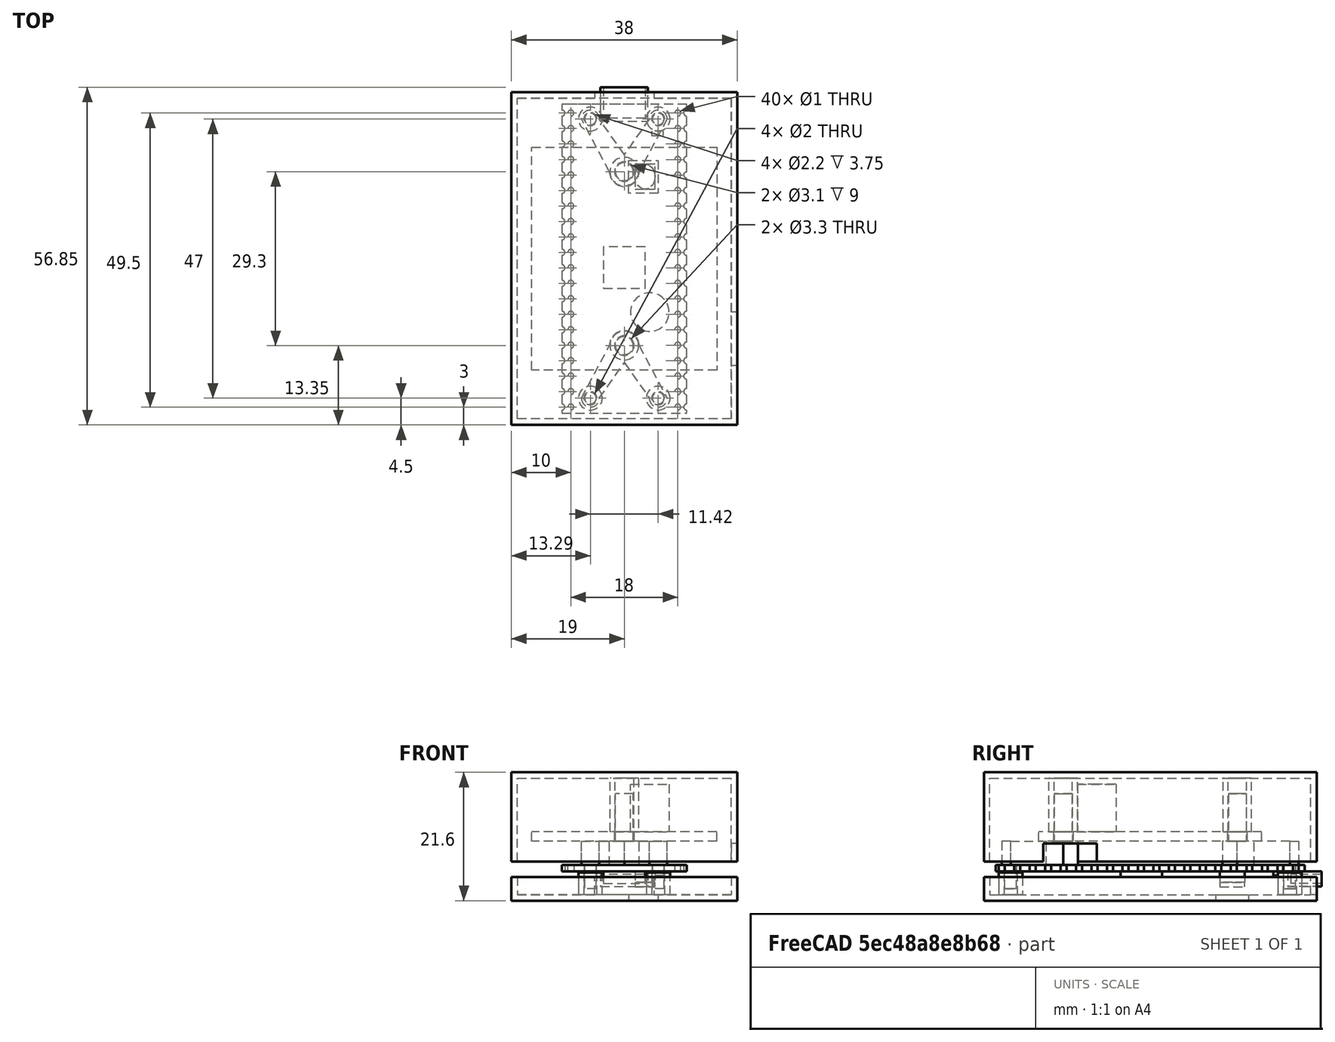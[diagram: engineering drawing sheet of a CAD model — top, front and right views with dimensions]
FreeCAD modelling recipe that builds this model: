
FCSTD DOCUMENT  (FreeCAD 0.19R24366 (Git))
Label: electronics_case
License: All rights reserved
LicenseURL: http://en.wikipedia.org/wiki/All_rights_reserved
objects: Sketcher::SketchObject×29, PartDesign::Pad×18, PartDesign::Pocket×11, PartDesign::Mirrored×7, PartDesign::Body×6, PartDesign::MultiTransform×3, Mesh::Feature×3, PartDesign::LinearPattern×2
note: 105 computed .brp shape members not serialized (recipe doc carries the construction recipe); baked Part::Feature solids carry a one-line shape summary decoded from their .brp

FEATURE [Sketcher::SketchObject] Sketch
  FullyConstrained = true
  MapMode = 5
  Support = -> [XY_Plane]
  sketch-geometry (4):
    g0: LineSegment StartX=-10.5 StartY=26 StartZ=0 EndX=10.5 EndY=26 EndZ=0
    g1: LineSegment StartX=10.5 StartY=26 StartZ=0 EndX=10.5 EndY=-26 EndZ=0
    g2: LineSegment StartX=10.5 StartY=-26 StartZ=0 EndX=-10.5 EndY=-26 EndZ=0
    g3: LineSegment StartX=-10.5 StartY=-26 StartZ=0 EndX=-10.5 EndY=26 EndZ=0
  constraints (11):
    c: Coincident(g0,g1)
    c: Coincident(g1,g2)
    c: Coincident(g2,g3)
    c: Coincident(g3,g0)
    c: Horizontal(g0)
    c: Horizontal(g2)
    c: Vertical(g1)
    c: Vertical(g3)
    c: Symmetric(g1,g0,g-1)
    c: DistanceY(g1,g1) = 52
    c: DistanceX(g0,g0) = 21
FEATURE [PartDesign::Pad] Pad
  Direction = (1,1,1)
  Length = 1.1
  Length2 = 100
  Profile = -> Sketch
  Refine = true
  Type = 0
FEATURE [Sketcher::SketchObject] Sketch001
  FullyConstrained = true
  MapMode = 5
  Placement = pos=(0,0,1.1) rot=(0,0,1;0rad)
  Support = -> [Pad]
  expr: Constraints[2] = 11.42 / 2
  sketch-geometry (1):
    g0: Circle CenterX=-5.71 CenterY=23.5 CenterZ=0 NormalX=0 NormalY=0 NormalZ=1 AngleXU=0 Radius=1
  constraints (3):
    c: Diameter(g0) = 2
    c: DistanceY(g-1,g0) = 23.5
    c: DistanceX(g0,g-1) = 5.71
FEATURE [PartDesign::Pocket] Pocket
  BaseFeature = -> Pad
  Length = 5
  Length2 = 100
  Profile = -> Sketch001
  Refine = true
  Type = 1
FEATURE [PartDesign::Mirrored] Mirrored
  MirrorPlane = -> Sketch001 [V_Axis]
  Refine = true
FEATURE [PartDesign::Mirrored] Mirrored001
  MirrorPlane = -> Sketch001 [H_Axis]
  Refine = true
FEATURE [PartDesign::MultiTransform] MultiTransform
  BaseFeature = -> Pocket
  Originals = -> [Pocket]
  Refine = true
  Transformations = -> [Mirrored,Mirrored001]
FEATURE [Sketcher::SketchObject] Sketch002
  ExternalGeometry = -> [MultiTransform]
  FullyConstrained = true
  MapMode = 5
  Support = -> [XY_Plane]
  sketch-geometry (5):
    g0: LineSegment StartX=-4 StartY=28.85 StartZ=0 EndX=4 EndY=28.85 EndZ=0
    g1: LineSegment StartX=4 StartY=28.85 StartZ=0 EndX=4 EndY=23.15 EndZ=0
    g2: LineSegment StartX=4 StartY=23.15 StartZ=0 EndX=-4 EndY=23.15 EndZ=0
    g3: LineSegment StartX=-4 StartY=23.15 StartZ=0 EndX=-4 EndY=28.85 EndZ=0
    g4: GeomPoint X=-2e-16 Y=26 Z=0
  constraints (12):
    c: Coincident(g0,g1)
    c: Coincident(g1,g2)
    c: Coincident(g2,g3)
    c: Coincident(g3,g0)
    c: Horizontal(g0)
    c: Horizontal(g2)
    c: Vertical(g1)
    c: Vertical(g3)
    c: Symmetric(g-3,g-3,g4)
    c: Symmetric(g1,g0,g4)
    c: DistanceX(g0,g0) = 8
    c: DistanceY(g3,g3) = 5.7
FEATURE [PartDesign::Pad] Pad001
  BaseFeature = -> MultiTransform
  Direction = (1,1,1)
  Length = 3.6
  Length2 = 100
  Profile = -> Sketch002
  Refine = true
  Type = 0
FEATURE [Sketcher::SketchObject] Sketch004
  ExternalGeometry = -> [Pad001]
  FullyConstrained = true
  MapMode = 5
  Placement = pos=(0,0,1.1) rot=(0,0,1;0rad)
  Support = -> [Pad001]
  sketch-geometry (4):
    g0: LineSegment StartX=-5.15 StartY=15.9 StartZ=0 EndX=-1.8 EndY=15.9 EndZ=0
    g1: LineSegment StartX=-1.8 StartY=15.9 StartZ=0 EndX=-1.8 EndY=11.7 EndZ=0
    g2: LineSegment StartX=-1.8 StartY=11.7 StartZ=0 EndX=-5.15 EndY=11.7 EndZ=0
    g3: LineSegment StartX=-5.15 StartY=11.7 StartZ=0 EndX=-5.15 EndY=15.9 EndZ=0
  constraints (12):
    c: Coincident(g0,g1)
    c: Coincident(g1,g2)
    c: Coincident(g2,g3)
    c: Coincident(g3,g0)
    c: Horizontal(g0)
    c: Horizontal(g2)
    c: Vertical(g1)
    c: Vertical(g3)
    c: DistanceY(g1,g1) = 4.2
    c: DistanceX(g0,g0) = 3.35
    c: DistanceX(g-3,g2) = 5.35
    c: DistanceY(g0,g-3) = 10.1
FEATURE [PartDesign::Pad] Pad002
  BaseFeature = -> Pad001
  Direction = (1,1,1)
  Length = 1.8
  Length2 = 100
  Profile = -> Sketch004
  Refine = true
  Type = 0
FEATURE [Sketcher::SketchObject] Sketch005
  ExternalGeometry = -> [Pad002]
  FullyConstrained = true
  MapMode = 5
  Placement = pos=(0,0,2.9) rot=(0,0,1;0rad)
  Support = -> [Pad002]
  sketch-geometry (5):
    g0: Ellipse CenterX=-3.475 CenterY=13.8 CenterZ=0 NormalX=0 NormalY=0 NormalZ=1 MajorRadius=2.1 MinorRadius=1.675 AngleXU=-1.5708
    g1: LineSegment StartX=-3.475 StartY=11.7 StartZ=0 EndX=-3.475 EndY=15.9 EndZ=0
    g2: LineSegment StartX=-1.8 StartY=13.8 StartZ=0 EndX=-5.15 EndY=13.8 EndZ=0
    g3: GeomPoint X=-3.475 Y=12.5334 Z=0
    g4: GeomPoint X=-3.475 Y=15.0666 Z=0
  constraints (4):
    c: InternalAlignment(g1-g4 -> g0) x4
    c: Symmetric(g-5,g-6,g0)
    c: Symmetric(g-6,g-5,g1)
    c: Symmetric(g-6,g-6,g2)
FEATURE [PartDesign::Pad] Pad003
  BaseFeature = -> Pad002
  Direction = (1,1,1)
  Length = 0.8
  Length2 = 100
  Profile = -> Sketch005
  Refine = true
  Type = 0
FEATURE [Sketcher::SketchObject] Sketch006
  ExternalGeometry = -> [Pad003]
  FullyConstrained = true
  MapMode = 5
  Placement = pos=(0,0,1.1) rot=(0,0,1;0rad)
  Support = -> [Pad003]
  sketch-geometry (4):
    g0: LineSegment StartX=-6.6 StartY=21.5 StartZ=0 EndX=-4.6 EndY=21.5 EndZ=0
    g1: LineSegment StartX=-4.6 StartY=21.5 StartZ=0 EndX=-4.6 EndY=20.7 EndZ=0
    g2: LineSegment StartX=-4.6 StartY=20.7 StartZ=0 EndX=-6.6 EndY=20.7 EndZ=0
    g3: LineSegment StartX=-6.6 StartY=20.7 StartZ=0 EndX=-6.6 EndY=21.5 EndZ=0
  constraints (12):
    c: Coincident(g0,g1)
    c: Coincident(g1,g2)
    c: Coincident(g2,g3)
    c: Coincident(g3,g0)
    c: Horizontal(g0)
    c: Horizontal(g2)
    c: Vertical(g1)
    c: Vertical(g3)
    c: DistanceX(g0,g0) = 2
    c: DistanceY(g3,g3) = 0.8
    c: DistanceX(g-3,g0) = 3.9
    c: DistanceY(g0,g-3) = 4.5
FEATURE [PartDesign::Pad] Pad004
  BaseFeature = -> Pad003
  Direction = (1,1,1)
  Length = 0.7
  Length2 = 100
  Profile = -> Sketch006
  Refine = true
  Type = 0
FEATURE [Sketcher::SketchObject] Sketch007
  ExternalGeometry = -> [Pad004]
  FullyConstrained = true
  MapMode = 5
  Placement = pos=(0,0,1.1) rot=(0,0,1;0rad)
  Support = -> [Pad004]
  sketch-geometry (4):
    g0: LineSegment StartX=-3.5 StartY=2 StartZ=0 EndX=3.5 EndY=2 EndZ=0
    g1: LineSegment StartX=3.5 StartY=2 StartZ=0 EndX=3.5 EndY=-5 EndZ=0
    g2: LineSegment StartX=3.5 StartY=-5 StartZ=0 EndX=-3.5 EndY=-5 EndZ=0
    g3: LineSegment StartX=-3.5 StartY=-5 StartZ=0 EndX=-3.5 EndY=2 EndZ=0
  constraints (12):
    c: Coincident(g0,g1)
    c: Coincident(g1,g2)
    c: Coincident(g2,g3)
    c: Coincident(g3,g0)
    c: Horizontal(g0)
    c: Horizontal(g2)
    c: Vertical(g1)
    c: Vertical(g3)
    c: DistanceY(g1,g1) = 7
    c: DistanceX(g0,g0) = 7
    c: DistanceX(g-3,g2) = 7
    c: DistanceY(g-3,g2) = 21
FEATURE [PartDesign::Pad] Pad005
  BaseFeature = -> Pad004
  Direction = (1,1,1)
  Length = 0.9
  Length2 = 100
  Profile = -> Sketch007
  Refine = true
  Type = 0
FEATURE [Sketcher::SketchObject] Sketch009
  ExternalGeometry = -> [Pad005]
  FullyConstrained = true
  MapMode = 5
  Support = -> [XY_Plane]
  sketch-geometry (1):
    g0: Circle CenterX=-9 CenterY=24.5 CenterZ=0 NormalX=0 NormalY=0 NormalZ=1 AngleXU=0 Radius=0.5
  constraints (3):
    c: Diameter(g0) = 1
    c: DistanceY(g0,g-3) = 1.5
    c: DistanceX(g-3,g0) = 1.5
FEATURE [PartDesign::Pocket] Pocket001
  BaseFeature = -> Pad005
  Length = 5
  Length2 = 100
  Profile = -> Sketch009
  Refine = true
  Reversed = true
  Type = 1
FEATURE [PartDesign::LinearPattern] LinearPattern
  Direction = -> Y_Axis
  Length = 49.5
  Occurrences = 20
  Refine = true
  Reversed = true
  expr: Length = 52 - 2.5
FEATURE [PartDesign::Mirrored] Mirrored002
  MirrorPlane = -> Sketch009 [V_Axis]
  Refine = true
FEATURE [PartDesign::MultiTransform] MultiTransform001
  BaseFeature = -> Pocket001
  Originals = -> [Pocket001]
  Refine = true
  Transformations = -> [LinearPattern,Mirrored002]
FEATURE [Sketcher::SketchObject] Sketch010
  ExternalGeometry = -> [MultiTransform001]
  FullyConstrained = true
  MapMode = 5
  Placement = pos=(0,0,1.1) rot=(0,0,1;0rad)
  Support = -> [MultiTransform001]
  sketch-geometry (1):
    g0: Circle CenterX=-10.5 CenterY=24.5 CenterZ=0 NormalX=0 NormalY=0 NormalZ=1 AngleXU=0 Radius=0.5
  constraints (3):
    c: Diameter(g0) = 1
    c: DistanceY(g0,g-3) = 1.5
    c: DistanceX(g0,g-3) = 0
FEATURE [PartDesign::Pocket] Pocket002
  BaseFeature = -> MultiTransform001
  Length = 5
  Length2 = 100
  Profile = -> Sketch010
  Refine = true
  Type = 1
FEATURE [PartDesign::LinearPattern] LinearPattern001
  Direction = -> Sketch010 [V_Axis]
  Length = 49.5
  Occurrences = 20
  Refine = true
  Reversed = true
  expr: Length = 52 - 2.5
FEATURE [PartDesign::Mirrored] Mirrored003
  MirrorPlane = -> Sketch010 [V_Axis]
  Refine = true
FEATURE [PartDesign::MultiTransform] MultiTransform002
  BaseFeature = -> Pocket002
  Originals = -> [Pocket002]
  Refine = true
  Transformations = -> [LinearPattern001,Mirrored003]
FEATURE [Sketcher::SketchObject] Sketch011
  ExternalGeometry = -> [MultiTransform002]
  FullyConstrained = true
  MapMode = 5
  Placement = pos=(0,28.85,0) rot=(0,0.707107,0.707107;3.14159rad)
  Support = -> [MultiTransform002]
  sketch-geometry (4):
    g0: LineSegment StartX=-3.5 StartY=3.1 StartZ=0 EndX=3.5 EndY=3.1 EndZ=0
    g1: LineSegment StartX=3.5 StartY=3.1 StartZ=0 EndX=3.5 EndY=1.6 EndZ=0
    g2: LineSegment StartX=3.5 StartY=1.6 StartZ=0 EndX=-3.5 EndY=1.6 EndZ=0
    g3: LineSegment StartX=-3.5 StartY=1.6 StartZ=0 EndX=-3.5 EndY=3.1 EndZ=0
  constraints (11):
    c: Coincident(g0,g1)
    c: Coincident(g1,g2)
    c: Coincident(g2,g3)
    c: Coincident(g3,g0)
    c: Horizontal(g2)
    c: Vertical(g1)
    c: Vertical(g3)
    c: Symmetric(g0,g0,g-2)
    c: DistanceY(g1,g1) = 1.5
    c: DistanceY(g0,g-3) = 0.5
    c: DistanceX(g-3,g0) = 0.5
FEATURE [PartDesign::Pocket] Pocket003
  BaseFeature = -> MultiTransform002
  Length = 5.2
  Length2 = 100
  Profile = -> Sketch011
  Refine = true
  Type = 0
FEATURE [Sketcher::SketchObject] Sketch012
  ExternalGeometry = -> [Pocket003]
  FullyConstrained = true
  MapMode = 5
  Placement = pos=(-4,0,0) rot=(0.57735,-0.57735,-0.57735;2.0944rad)
  Support = -> [Pocket003]
  sketch-geometry (4):
    g0: LineSegment StartX=-28.85 StartY=0 StartZ=0 EndX=-26 EndY=0 EndZ=0
    g1: LineSegment StartX=-26 StartY=0 StartZ=0 EndX=-26 EndY=1.1 EndZ=0
    g2: LineSegment StartX=-26 StartY=1.1 StartZ=0 EndX=-28.85 EndY=1.1 EndZ=0
    g3: LineSegment StartX=-28.85 StartY=1.1 StartZ=0 EndX=-28.85 EndY=0 EndZ=0
  constraints (9):
    c: Coincident(g-4,g0)
    c: Coincident(g0,g-5)
    c: Coincident(g0,g1)
    c: Coincident(g1,g-5)
    c: Coincident(g1,g2)
    c: PointOnObject(g2,g-4)
    c: Horizontal(g2)
    c: Coincident(g2,g3)
    c: Coincident(g3,g0)
FEATURE [PartDesign::Pocket] Pocket004
  BaseFeature = -> Pocket003
  Length = 5
  Length2 = 100
  Profile = -> Sketch012
  Refine = true
  Type = 1
FEATURE [PartDesign::Body] Body  label="pico"
  Group = -> [Sketch,Pad,Sketch001,Pocket,MultiTransform,Mirrored,Mirrored001,Sketch002,Pad001,Sketch004,Pad002,Sketch005,Pad003,Sketch006,Pad004,Sketch007,Pad005,Sketch009,Pocket001,MultiTransform001,LinearPattern,Mirrored002,Sketch010,Pocket002,MultiTransform002,LinearPattern001,Mirrored003,Sketch011,Pocket003,Sketch012,Pocket004]
  Origin = -> Origin
  Placement = pos=(1e-15,-3e-15,6) rot=(0,1,0;3.14159rad)
  Tip = -> Pocket004
FEATURE [Sketcher::SketchObject] Sketch018
  FullyConstrained = true
  MapMode = 5
  Support = -> [XY_Plane004]
  sketch-geometry (4):
    g0: LineSegment StartX=-15.56 StartY=18.75 StartZ=0 EndX=15.56 EndY=18.75 EndZ=0
    g1: LineSegment StartX=15.56 StartY=18.75 StartZ=0 EndX=15.56 EndY=-18.75 EndZ=0
    g2: LineSegment StartX=15.56 StartY=-18.75 StartZ=0 EndX=-15.56 EndY=-18.75 EndZ=0
    g3: LineSegment StartX=-15.56 StartY=-18.75 StartZ=0 EndX=-15.56 EndY=18.75 EndZ=0
  constraints (11):
    c: Coincident(g0,g1)
    c: Coincident(g1,g2)
    c: Coincident(g2,g3)
    c: Coincident(g3,g0)
    c: Horizontal(g0)
    c: Horizontal(g2)
    c: Vertical(g1)
    c: Vertical(g3)
    c: Symmetric(g1,g0,g-1)
    c: DistanceY(g1,g1) = 37.5
    c: DistanceX(g0,g0) = 31.12
FEATURE [PartDesign::Pad] Pad010
  Direction = (1,1,1)
  Length = 1.6
  Length2 = 100
  Profile = -> Sketch018
  Refine = true
  Type = 0
FEATURE [Sketcher::SketchObject] Sketch019
  FullyConstrained = true
  MapMode = 5
  Placement = pos=(0,0,0) rot=(1,0,0;3.14159rad)
  Support = -> [Pad010]
  expr: Constraints[1] = 29.3 / 2
  sketch-geometry (1):
    g0: Circle CenterX=0 CenterY=14.65 CenterZ=0 NormalX=0 NormalY=0 NormalZ=1 AngleXU=0 Radius=1.65
  constraints (3):
    c: PointOnObject(g0,g-2)
    c: DistanceY(g0) = 14.65
    c: Radius(g0) = 1.65
FEATURE [PartDesign::Pocket] Pocket006
  BaseFeature = -> Pad010
  Length = 5
  Length2 = 100
  Profile = -> Sketch019
  Refine = true
  Type = 1
FEATURE [PartDesign::Mirrored] Mirrored008
  BaseFeature = -> Pocket006
  MirrorPlane = -> Sketch019 [H_Axis]
  Originals = -> [Pocket006]
  Refine = true
FEATURE [Sketcher::SketchObject] Sketch024
  FullyConstrained = true
  MapMode = 5
  Support = -> [XY_Plane005]
  sketch-geometry (7):
    g0: ArcOfCircle CenterX=5.71 CenterY=0 CenterZ=0 NormalX=0 NormalY=0 NormalZ=1 AngleXU=0 Radius=1.5 StartAngle=3.14159 EndAngle=6.28319
    g1: ArcOfCircle CenterX=-5.71 CenterY=0 CenterZ=0 NormalX=0 NormalY=0 NormalZ=1 AngleXU=0 Radius=1.5 StartAngle=3.14159 EndAngle=6.28319
    g2: ArcOfCircle CenterX=0 CenterY=8.85 CenterZ=0 NormalX=0 NormalY=0 NormalZ=1 AngleXU=0 Radius=2.5 StartAngle=4.75696e-06 EndAngle=3.14159
    g3: LineSegment StartX=-7.21 StartY=2e-16 StartZ=0 EndX=-2.5 EndY=8.85001 EndZ=0
    g4: LineSegment StartX=2.5 StartY=8.85001 StartZ=0 EndX=7.21 EndY=0 EndZ=0
    g5: LineSegment StartX=-4.21 StartY=-4e-16 StartZ=0 EndX=0 EndY=6 EndZ=0
    g6: LineSegment StartX=0 StartY=6 StartZ=0 EndX=4.21 EndY=0 EndZ=0
  constraints (23):
    c: PointOnObject(g0,g-1)
    c: Radius(g0) = 1.5
    c: Equal(g0,g1)
    c: Symmetric(g1,g0,g-1)
    c: DistanceX(g0) = 5.71
    c: PointOnObject(g2,g-2)
    c: Radius(g2) = 2.5
    c: DistanceY(g2) = 8.85
    c: Horizontal(g3,g4)
    c: DistanceX(g3) = -2.5
    c: DistanceY(g4) = 0
    c: DistanceY(g-1,g3) = 0
    c: PointOnObject(g5,g-2)
    c: Coincident(g5,g6)
    c: DistanceY(g6) = 0
    c: DistanceY(g5) = 0
    c: DistanceY(g5) = 6
    c: Coincident(g1,g5)
    c: Coincident(g0,g6)
    c: Coincident(g2,g4)
    c: Coincident(g2,g3)
    c: Coincident(g1,g3)
    c: Coincident(g0,g4)
FEATURE [PartDesign::Pad] Pad011
  Direction = (1,1,1)
  Length = 4
  Length2 = 100
  Profile = -> Sketch024
  Refine = true
  Type = 0
FEATURE [Sketcher::SketchObject] Sketch025
  ExternalGeometry = -> [Pad011]
  FullyConstrained = true
  MapMode = 5
  Placement = pos=(0,0,4) rot=(0,0,1;0rad)
  Support = -> [Pad011]
  sketch-geometry (1):
    g0: Circle CenterX=0 CenterY=8.85 CenterZ=0 NormalX=0 NormalY=0 NormalZ=1 AngleXU=0 Radius=1.5
  constraints (2):
    c: Coincident(g0,g-3)
    c: Radius(g0) = 1.5
FEATURE [PartDesign::Pad] Pad012
  BaseFeature = -> Pad011
  Direction = (1,1,1)
  Length = 8
  Length2 = 100
  Profile = -> Sketch025
  Refine = true
  Type = 0
FEATURE [Sketcher::SketchObject] Sketch026
  ExternalGeometry = -> [Pad012]
  FullyConstrained = true
  MapMode = 5
  Placement = pos=(0,0,0) rot=(1,0,0;3.14159rad)
  Support = -> [Pad012]
  sketch-geometry (2):
    g0: Circle CenterX=-5.71 CenterY=0 CenterZ=0 NormalX=0 NormalY=0 NormalZ=1 AngleXU=0 Radius=0.975
    g1: Circle CenterX=5.71 CenterY=0 CenterZ=0 NormalX=0 NormalY=0 NormalZ=1 AngleXU=0 Radius=0.975
  constraints (4):
    c: Coincident(g0,g-3)
    c: Radius(g0) = 0.975
    c: Coincident(g1,g-4)
    c: Equal(g0,g1)
FEATURE [PartDesign::Pad] Pad013
  BaseFeature = -> Pad012
  Direction = (1,1,1)
  Length = 4
  Length2 = 100
  Profile = -> Sketch026
  Refine = true
  Type = 0
FEATURE [PartDesign::Body] Body004  label="strut"
  Group = -> [Sketch024,Pad011,Sketch025,Pad012,Sketch026,Pad013]
  Origin = -> Origin005
  Placement = pos=(0,-23.5,6) rot=(0,0,1;0rad)
  Tip = -> Pad013
FEATURE [Sketcher::SketchObject] Sketch028
  FullyConstrained = true
  MapMode = 5
  Support = -> [XY_Plane006]
  sketch-geometry (7):
    g0: ArcOfCircle CenterX=5.71 CenterY=0 CenterZ=0 NormalX=0 NormalY=0 NormalZ=1 AngleXU=0 Radius=1.5 StartAngle=3.14159 EndAngle=6.28319
    g1: ArcOfCircle CenterX=-5.71 CenterY=0 CenterZ=0 NormalX=0 NormalY=0 NormalZ=1 AngleXU=0 Radius=1.5 StartAngle=3.14159 EndAngle=6.28319
    g2: ArcOfCircle CenterX=0 CenterY=8.85 CenterZ=0 NormalX=0 NormalY=0 NormalZ=1 AngleXU=0 Radius=2.5 StartAngle=4.75696e-06 EndAngle=3.14159
    g3: LineSegment StartX=-7.21 StartY=2e-16 StartZ=0 EndX=-2.5 EndY=8.85001 EndZ=0
    g4: LineSegment StartX=2.5 StartY=8.85001 StartZ=0 EndX=7.21 EndY=0 EndZ=0
    g5: LineSegment StartX=-4.21 StartY=-4e-16 StartZ=0 EndX=0 EndY=6 EndZ=0
    g6: LineSegment StartX=0 StartY=6 StartZ=0 EndX=4.21 EndY=0 EndZ=0
  constraints (23):
    c: PointOnObject(g0,g-1)
    c: Radius(g0) = 1.5
    c: Equal(g0,g1)
    c: Symmetric(g1,g0,g-1)
    c: DistanceX(g0) = 5.71
    c: PointOnObject(g2,g-2)
    c: Radius(g2) = 2.5
    c: DistanceY(g2) = 8.85
    c: Horizontal(g3,g4)
    c: DistanceX(g3) = -2.5
    c: DistanceY(g4) = 0
    c: DistanceY(g-1,g3) = 0
    c: PointOnObject(g5,g-2)
    c: Coincident(g5,g6)
    c: DistanceY(g6) = 0
    c: DistanceY(g5) = 0
    c: DistanceY(g5) = 6
    c: Coincident(g1,g5)
    c: Coincident(g0,g6)
    c: Coincident(g2,g4)
    c: Coincident(g2,g3)
    c: Coincident(g1,g3)
    c: Coincident(g0,g4)
FEATURE [PartDesign::Pad] Pad014
  Direction = (1,1,1)
  Length = 4
  Length2 = 100
  Profile = -> Sketch028
  Refine = true
  Type = 0
FEATURE [Sketcher::SketchObject] Sketch029
  ExternalGeometry = -> [Pad014]
  FullyConstrained = true
  MapMode = 5
  Placement = pos=(0,0,4) rot=(0,0,1;0rad)
  Support = -> [Pad014]
  sketch-geometry (1):
    g0: Circle CenterX=0 CenterY=8.85 CenterZ=0 NormalX=0 NormalY=0 NormalZ=1 AngleXU=0 Radius=1.5
  constraints (2):
    c: Coincident(g0,g-3)
    c: Radius(g0) = 1.5
FEATURE [PartDesign::Pad] Pad016
  BaseFeature = -> Pad014
  Direction = (1,1,1)
  Length = 8
  Length2 = 100
  Profile = -> Sketch029
  Refine = true
  Type = 0
FEATURE [Sketcher::SketchObject] Sketch027
  ExternalGeometry = -> [Pad016]
  FullyConstrained = true
  MapMode = 5
  Placement = pos=(0,0,0) rot=(1,0,0;3.14159rad)
  Support = -> [Pad016]
  sketch-geometry (2):
    g0: Circle CenterX=-5.71 CenterY=0 CenterZ=0 NormalX=0 NormalY=0 NormalZ=1 AngleXU=0 Radius=0.975
    g1: Circle CenterX=5.71 CenterY=0 CenterZ=0 NormalX=0 NormalY=0 NormalZ=1 AngleXU=0 Radius=0.975
  constraints (4):
    c: Coincident(g0,g-3)
    c: Radius(g0) = 0.975
    c: Coincident(g1,g-4)
    c: Equal(g0,g1)
FEATURE [PartDesign::Pad] Pad015
  BaseFeature = -> Pad016
  Direction = (1,1,1)
  Length = 4
  Length2 = 100
  Profile = -> Sketch027
  Refine = true
  Type = 0
FEATURE [PartDesign::Body] Body005  label="strut2"
  Group = -> [Sketch028,Pad014,Sketch029,Pad016,Sketch027,Pad015]
  Origin = -> Origin006
  Placement = pos=(-5e-15,23.5,6) rot=(0,0,1;3.14159rad)
  Tip = -> Pad015
FEATURE [Sketcher::SketchObject] Sketch030
  FullyConstrained = true
  MapMode = 5
  Support = -> [XY_Plane008]
  sketch-geometry (4):
    g0: LineSegment StartX=-19 StartY=28 StartZ=0 EndX=19 EndY=28 EndZ=0
    g1: LineSegment StartX=19 StartY=28 StartZ=0 EndX=19 EndY=-28 EndZ=0
    g2: LineSegment StartX=19 StartY=-28 StartZ=0 EndX=-19 EndY=-28 EndZ=0
    g3: LineSegment StartX=-19 StartY=-28 StartZ=0 EndX=-19 EndY=28 EndZ=0
  constraints (11):
    c: Coincident(g0,g1)
    c: Coincident(g1,g2)
    c: Coincident(g2,g3)
    c: Coincident(g3,g0)
    c: Horizontal(g0)
    c: Horizontal(g2)
    c: Vertical(g1)
    c: Vertical(g3)
    c: Symmetric(g1,g0,g-1)
    c: DistanceY(g3,g3) = 56
    c: DistanceX(g2,g2) = 38
FEATURE [PartDesign::Pad] Pad017
  Direction = (1,1,1)
  Length = 15
  Length2 = 100
  Profile = -> Sketch030
  Refine = true
  Type = 0
FEATURE [Sketcher::SketchObject] Sketch031
  FullyConstrained = true
  MapMode = 5
  Placement = pos=(0,0,0) rot=(1,0,0;3.14159rad)
  Support = -> [Pad017]
  sketch-geometry (4):
    g0: LineSegment StartX=-18 StartY=27 StartZ=0 EndX=18 EndY=27 EndZ=0
    g1: LineSegment StartX=18 StartY=27 StartZ=0 EndX=18 EndY=-27 EndZ=0
    g2: LineSegment StartX=18 StartY=-27 StartZ=0 EndX=-18 EndY=-27 EndZ=0
    g3: LineSegment StartX=-18 StartY=-27 StartZ=0 EndX=-18 EndY=27 EndZ=0
  constraints (11):
    c: Coincident(g0,g1)
    c: Coincident(g1,g2)
    c: Coincident(g2,g3)
    c: Coincident(g3,g0)
    c: Horizontal(g0)
    c: Horizontal(g2)
    c: Vertical(g1)
    c: Vertical(g3)
    c: Symmetric(g0,g1,g-1)
    c: DistanceY(g3,g3) = 54
    c: DistanceX(g2,g2) = 36
FEATURE [PartDesign::Pocket] Pocket007
  BaseFeature = -> Pad017
  Length = 14
  Length2 = 100
  Profile = -> Sketch031
  Refine = true
  Type = 0
FEATURE [Sketcher::SketchObject] Sketch032
  FullyConstrained = true
  MapMode = 5
  Placement = pos=(0,0,1.6) rot=(0,0,1;0rad)
  Support = -> [Mirrored008]
  sketch-geometry (1):
    g0: Circle CenterX=-4.29699 CenterY=9.00655 CenterZ=0 NormalX=0 NormalY=0 NormalZ=1 AngleXU=0 Radius=3.25
  constraints (3):
    c: Radius(g0) = 3.25
    c: DistanceX(g0) = -4.29699
    c: DistanceY(g0) = 9.00655
FEATURE [PartDesign::Pad] Pad018
  BaseFeature = -> Mirrored008
  Direction = (1,1,1)
  Length = 8
  Length2 = 100
  Profile = -> Sketch032
  Refine = true
  Type = 0
FEATURE [PartDesign::Body] Body003  label="BED"
  Group = -> [Sketch018,Pad010,Sketch019,Pocket006,Mirrored008,Sketch032,Pad018]
  Origin = -> Origin004
  Placement = pos=(0,0,10) rot=(0,0,1;3.14159rad)
  Tip = -> Pad018
FEATURE [Sketcher::SketchObject] Sketch033
  FullyConstrained = true
  MapMode = 5
  Placement = pos=(0,0,14) rot=(1,0,0;3.14159rad)
  Support = -> [Pocket007]
  sketch-geometry (2):
    g0: Circle CenterX=0 CenterY=14.65 CenterZ=0 NormalX=0 NormalY=0 NormalZ=1 AngleXU=0 Radius=2.4
    g1: Circle CenterX=0 CenterY=14.65 CenterZ=0 NormalX=0 NormalY=0 NormalZ=1 AngleXU=0 Radius=1.55
  constraints (5):
    c: PointOnObject(g0,g-2)
    c: Radius(g0) = 2.4
    c: Coincident(g1,g0)
    c: Radius(g1) = 1.55
    c: DistanceY(g0) = 14.65
FEATURE [PartDesign::Pad] Pad019
  BaseFeature = -> Pocket007
  Direction = (1,1,1)
  Length = 9
  Length2 = 100
  Profile = -> Sketch033
  Refine = true
  Type = 0
FEATURE [PartDesign::Mirrored] Mirrored009
  BaseFeature = -> Pad019
  MirrorPlane = -> XZ_Plane008
  Originals = -> [Pad019]
  Refine = true
FEATURE [Sketcher::SketchObject] Sketch034
  FullyConstrained = true
  MapMode = 5
  Support = -> [XY_Plane009]
  sketch-geometry (4):
    g0: LineSegment StartX=-19 StartY=28 StartZ=0 EndX=19 EndY=28 EndZ=0
    g1: LineSegment StartX=19 StartY=28 StartZ=0 EndX=19 EndY=-28 EndZ=0
    g2: LineSegment StartX=19 StartY=-28 StartZ=0 EndX=-19 EndY=-28 EndZ=0
    g3: LineSegment StartX=-19 StartY=-28 StartZ=0 EndX=-19 EndY=28 EndZ=0
  constraints (11):
    c: Coincident(g0,g1)
    c: Coincident(g1,g2)
    c: Coincident(g2,g3)
    c: Coincident(g3,g0)
    c: Horizontal(g0)
    c: Horizontal(g2)
    c: Vertical(g1)
    c: Vertical(g3)
    c: Symmetric(g1,g0,g-1)
    c: DistanceX(g0,g0) = 38
    c: DistanceY(g3,g3) = 56
FEATURE [PartDesign::Pad] Pad020
  Direction = (1,1,1)
  Length = 4
  Length2 = 100
  Profile = -> Sketch034
  Refine = true
  Type = 0
FEATURE [Sketcher::SketchObject] Sketch035
  FullyConstrained = true
  MapMode = 5
  Placement = pos=(0,0,4) rot=(0,0,1;0rad)
  Support = -> [Pad020]
  sketch-geometry (4):
    g0: LineSegment StartX=-18 StartY=27 StartZ=0 EndX=18 EndY=27 EndZ=0
    g1: LineSegment StartX=18 StartY=27 StartZ=0 EndX=18 EndY=-27 EndZ=0
    g2: LineSegment StartX=18 StartY=-27 StartZ=0 EndX=-18 EndY=-27 EndZ=0
    g3: LineSegment StartX=-18 StartY=-27 StartZ=0 EndX=-18 EndY=27 EndZ=0
  constraints (11):
    c: Coincident(g0,g1)
    c: Coincident(g1,g2)
    c: Coincident(g2,g3)
    c: Coincident(g3,g0)
    c: Horizontal(g0)
    c: Horizontal(g2)
    c: Vertical(g1)
    c: Vertical(g3)
    c: Symmetric(g1,g0,g-1)
    c: DistanceY(g1,g1) = 54
    c: DistanceX(g2,g2) = 36
FEATURE [PartDesign::Pocket] Pocket008
  BaseFeature = -> Pad020
  Length = 3
  Length2 = 100
  Profile = -> Sketch035
  Refine = true
  Type = 0
FEATURE [Sketcher::SketchObject] Sketch036
  ExternalGeometry = -> [Pocket008]
  FullyConstrained = true
  MapMode = 5
  Placement = pos=(0,28,0) rot=(0,0.707107,0.707107;3.14159rad)
  Support = -> [Pocket008]
  sketch-geometry (4):
    g0: LineSegment StartX=-5 StartY=1 StartZ=0 EndX=5 EndY=1 EndZ=0
    g1: LineSegment StartX=5 StartY=1 StartZ=0 EndX=5 EndY=4 EndZ=0
    g2: LineSegment StartX=5 StartY=4 StartZ=0 EndX=-5 EndY=4 EndZ=0
    g3: LineSegment StartX=-5 StartY=4 StartZ=0 EndX=-5 EndY=1 EndZ=0
  constraints (11):
    c: Coincident(g0,g1)
    c: Coincident(g1,g2)
    c: Coincident(g2,g3)
    c: Coincident(g3,g0)
    c: Horizontal(g2)
    c: Vertical(g1)
    c: Vertical(g3)
    c: Symmetric(g0,g0,g-2)
    c: DistanceY(g2,g-3) = 0
    c: DistanceY(g3,g3) = 3
    c: DistanceX(g2,g2) = 10
FEATURE [PartDesign::Pocket] Pocket009
  BaseFeature = -> Pocket008
  Length = 5
  Length2 = 100
  Profile = -> Sketch036
  Refine = true
  Type = 0
FEATURE [Sketcher::SketchObject] Sketch037
  FullyConstrained = true
  MapMode = 5
  Placement = pos=(0,0,1) rot=(0,0,1;0rad)
  Support = -> [Pocket009]
  sketch-geometry (4):
    g0: Circle CenterX=-5.71 CenterY=23.5 CenterZ=0 NormalX=0 NormalY=0 NormalZ=1 AngleXU=0 Radius=2
    g1: Circle CenterX=5.71 CenterY=23.5 CenterZ=0 NormalX=0 NormalY=0 NormalZ=1 AngleXU=0 Radius=2
    g2: Circle CenterX=-5.71 CenterY=23.5 CenterZ=0 NormalX=0 NormalY=0 NormalZ=1 AngleXU=0 Radius=1.1
    g3: Circle CenterX=5.71 CenterY=23.5 CenterZ=0 NormalX=0 NormalY=0 NormalZ=1 AngleXU=0 Radius=1.1
  constraints (9):
    c: Equal(g1,g0)
    c: Radius(g0) = 2
    c: Coincident(g2,g0)
    c: Coincident(g3,g1)
    c: Equal(g3,g2)
    c: Radius(g2) = 1.1
    c: Symmetric(g1,g0,g-2)
    c: DistanceX(g0) = -5.71
    c: DistanceY(g0) = 23.5
FEATURE [PartDesign::Pad] Pad021
  BaseFeature = -> Pocket009
  Direction = (1,1,1)
  Length = 3.75
  Length2 = 100
  Profile = -> Sketch037
  Refine = true
  Type = 0
FEATURE [PartDesign::Mirrored] Mirrored010
  BaseFeature = -> Pad021
  MirrorPlane = -> XZ_Plane009
  Originals = -> [Pad021]
  Refine = true
FEATURE [Sketcher::SketchObject] Sketch038
  ExternalGeometry = -> [Mirrored009]
  FullyConstrained = true
  MapMode = 5
  Placement = pos=(19,0,0) rot=(0.57735,0.57735,0.57735;2.0944rad)
  Support = -> [Mirrored009]
  sketch-geometry (4):
    g0: LineSegment StartX=-18 StartY=0 StartZ=0 EndX=-9 EndY=0 EndZ=0
    g1: LineSegment StartX=-9 StartY=0 StartZ=0 EndX=-9 EndY=3 EndZ=0
    g2: LineSegment StartX=-9 StartY=3 StartZ=0 EndX=-18 EndY=3 EndZ=0
    g3: LineSegment StartX=-18 StartY=3 StartZ=0 EndX=-18 EndY=0 EndZ=0
  constraints (12):
    c: Coincident(g0,g1)
    c: Coincident(g1,g2)
    c: Coincident(g2,g3)
    c: Coincident(g3,g0)
    c: Horizontal(g0)
    c: Horizontal(g2)
    c: Vertical(g1)
    c: Vertical(g3)
    c: PointOnObject(g0,g-3)
    c: DistanceX(g2,g2) = 9
    c: DistanceY(g1,g1) = 3
    c: DistanceX(g0) = -9
FEATURE [PartDesign::Pocket] Pocket010
  BaseFeature = -> Mirrored009
  Length = 5
  Length2 = 100
  Profile = -> Sketch038
  Refine = true
  Type = 0
FEATURE [PartDesign::Body] Body007  label="case_top"
  Group = -> [Sketch030,Pad017,Sketch031,Pocket007,Sketch033,Pad019,Mirrored009,Sketch038,Pocket010]
  Origin = -> Origin008
  Placement = pos=(0,0,6.6) rot=(0,0,1;0rad)
  Tip = -> Pocket010
FEATURE [Sketcher::SketchObject] Sketch039
  ExternalGeometry = -> [Mirrored010]
  FullyConstrained = true
  MapMode = 5
  Placement = pos=(0,0,1) rot=(0,0,1;0rad)
  Support = -> [Mirrored010]
  sketch-geometry (4):
    g0: LineSegment StartX=5.71 StartY=16.5 StartZ=0 EndX=0.71 EndY=16.5 EndZ=0
    g1: LineSegment StartX=0.71 StartY=16.5 StartZ=0 EndX=0.71 EndY=11 EndZ=0
    g2: LineSegment StartX=0.71 StartY=11 StartZ=0 EndX=5.71 EndY=11 EndZ=0
    g3: LineSegment StartX=5.71 StartY=11 StartZ=0 EndX=5.71 EndY=16.5 EndZ=0
  constraints (12):
    c: Coincident(g0,g1)
    c: Coincident(g1,g2)
    c: Coincident(g2,g3)
    c: Coincident(g3,g0)
    c: Horizontal(g0)
    c: Horizontal(g2)
    c: Vertical(g1)
    c: Vertical(g3)
    c: DistanceY(g0,g-3) = 7
    c: DistanceX(g0,g0) = 5
    c: DistanceY(g3,g3) = 5.5
    c: DistanceX(g-3,g0) = 0
FEATURE [PartDesign::Pocket] Pocket011
  BaseFeature = -> Mirrored010
  Length = 5
  Length2 = 100
  Profile = -> Sketch039
  Refine = true
  Type = 0
FEATURE [PartDesign::Body] Body008  label="case_bottom"
  Group = -> [Sketch034,Pad020,Sketch035,Pocket008,Sketch036,Pocket009,Sketch037,Pad021,Mirrored010,Sketch039,Pocket011]
  Origin = -> Origin009
  Tip = -> Pocket011
FEATURE [Mesh::Feature] Mesh  label="strut_mesh"
FEATURE [Mesh::Feature] Mesh001  label="case_top_mesh"
FEATURE [Mesh::Feature] Mesh002  label="case_bottom_mesh"
